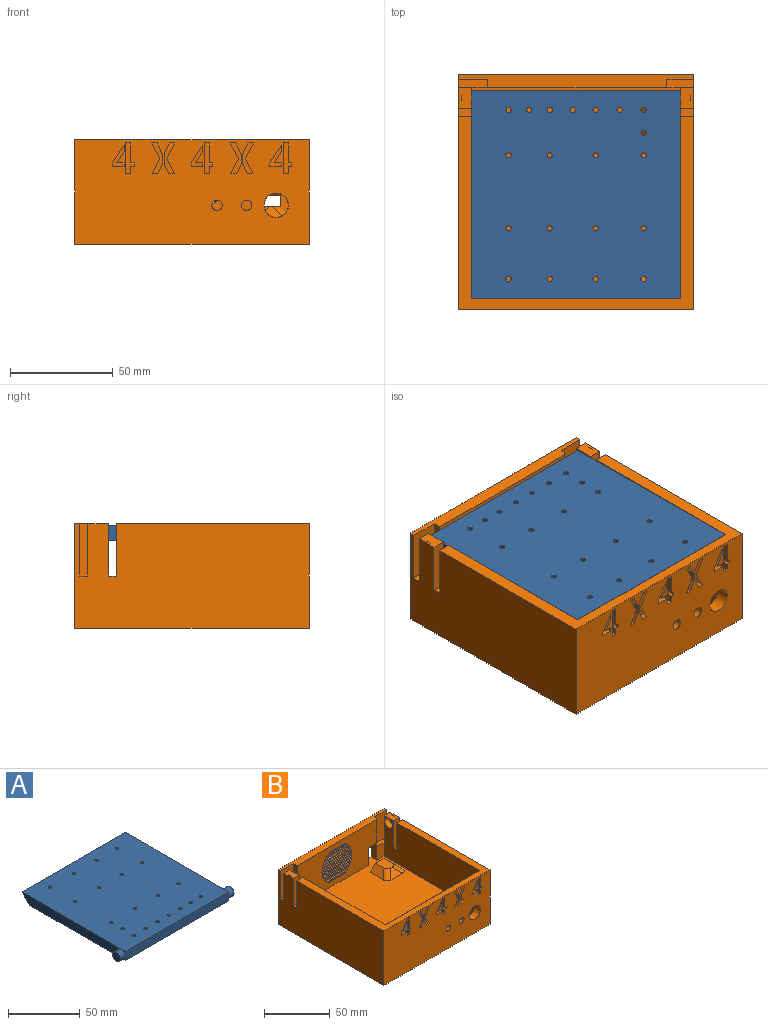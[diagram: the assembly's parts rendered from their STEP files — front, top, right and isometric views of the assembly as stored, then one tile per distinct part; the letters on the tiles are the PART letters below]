
ASSEMBLY  parts=2 mates=1
PART A: 34 faces, bbox 111.8x101.6x7.6 mm
  f0: plane 3.81x3.81mm, normal (-1,0,0), area 3.1mm2, adj f5,f24,f31
  f1: plane 3.81x3.81mm, normal (-1,0,0), area 3.1mm2, adj f5,f23,f31
  f2: plane 3.81x3.81mm, normal (1,0,0), area 3.1mm2, adj f5,f24,f30
  f3: plane 3.81x3.81mm, normal (1,0,0), area 3.1mm2, adj f5,f23,f30
  f4: plane 97.79x7.62mm, normal (-1,0,0), area 693.3mm2, adj f23,f24,f31,f33
  f5: plane 101.6x7.62mm, normal (0,-1,0), area 774.2mm2, adj f0,f1,f2,f3,f23,f24
  f6: plane 97.79x7.62mm, normal (1,0,0), area 693.3mm2, adj f23,f24,f30,f33
  f7: cylinder r=1.27mm len=7.62mm, axis (0,0,-1), area 60.8mm2, adj f23,f24
  f8: cylinder r=1.27mm len=7.62mm, axis (0,0,-1), area 60.8mm2, adj f23,f24
  f9: cylinder r=1.27mm len=7.62mm, axis (0,0,-1), area 60.8mm2, adj f23,f24
  f10: cylinder r=1.27mm len=7.62mm, axis (0,0,-1), area 60.8mm2, adj f23,f24
  f11: cylinder r=1.27mm len=7.62mm, axis (0,0,-1), area 60.8mm2, adj f23,f24
  f12: cylinder r=1.27mm len=7.62mm, axis (0,0,-1), area 60.8mm2, adj f23,f24
  f13: cylinder r=1.27mm len=7.62mm, axis (0,0,-1), area 60.8mm2, adj f23,f24
  f14: cylinder r=1.27mm len=7.62mm, axis (0,0,-1), area 60.8mm2, adj f23,f24
  f15: cylinder r=1.27mm len=7.62mm, axis (0,0,-1), area 60.8mm2, adj f23,f24
  f16: cylinder r=1.27mm len=7.62mm, axis (0,0,-1), area 60.8mm2, adj f23,f24
  f17: cylinder r=1.27mm len=7.62mm, axis (0,0,-1), area 60.8mm2, adj f23,f24
  f18: cylinder r=1.27mm len=7.62mm, axis (0,0,-1), area 60.8mm2, adj f23,f24
  f19: cylinder r=1.27mm len=7.62mm, axis (0,0,-1), area 60.8mm2, adj f23,f24
  f20: cylinder r=1.27mm len=7.62mm, axis (0,0,-1), area 60.8mm2, adj f23,f24
  f21: cylinder r=1.27mm len=7.62mm, axis (0,0,-1), area 60.8mm2, adj f23,f24
  f22: cylinder r=1.27mm len=7.62mm, axis (0,0,-1), area 60.8mm2, adj f23,f24
  f23: plane 101.6x101.6mm, normal (0,0,1), area 10221.2mm2, adj f1,f3,f4,f5,f6,f7,f8,f9
  f24: plane 101.6x93.98mm, normal (0,0,-1), area 9447mm2, adj f0,f2,f4,f5,f6,f7,f8,f9
  f25: cylinder r=1.27mm len=7.62mm, axis (0,0,1), area 60.8mm2, adj f23,f24
  f26: cylinder r=1.27mm len=7.62mm, axis (0,0,1), area 60.8mm2, adj f23,f24
  f27: cylinder r=1.27mm len=7.62mm, axis (0,0,1), area 60.8mm2, adj f23,f24
  f28: cylinder r=1.27mm len=7.62mm, axis (0,0,1), area 60.8mm2, adj f23,f24
  f29: plane 7.62x7.62mm, normal (1,0,0), area 45.6mm2, adj f30
  f30: cylinder r=3.81mm len=7.62mm, axis (1,0,0), area 121.6mm2, adj f2,f3,f6,f29
  f31: cylinder r=3.81mm len=7.62mm, axis (1,0,0), area 121.6mm2, adj f0,f1,f4,f32
  f32: plane 7.62x7.62mm, normal (-1,0,0), area 45.6mm2, adj f31
  f33: plane 101.6x7.62mm, normal (0,0.71,-0.71), area 1094.9mm2, adj f4,f6,f23,f24
PART B: 226 faces, bbox 114.3x114.3x50.8 mm
  f0: plane 100.33x33.02mm, normal (0,1,0), area 3010.1mm2, adj f1,f2,f8,f12,f54,f199,f200,f202
  f1: plane 8.71x5.08mm, normal (1,0,0), area 27.1mm2, adj f0,f203,f204,f212,f225
  f2: plane 8.71x5.08mm, normal (-1,0,0), area 27.1mm2, adj f0,f206,f213,f214,f225
  f3: plane 114.3x50.8mm, normal (-1,0,0), area 5612.9mm2, adj f4,f5,f9,f11,f15,f24,f42,f43
  f4: plane 114.3x6.35mm, normal (0,0,1), area 622.1mm2, adj f3,f7,f11,f23,f45,f53,f221,f222
  f5: plane 114.3x93.98mm, normal (0,0,1), area 1709.7mm2, adj f3,f6,f9,f12,f23,f55,f220,f223
  f6: plane 102.87x38.1mm, normal (-1,0,0), area 3595.4mm2, adj f5,f8,f10,f14,f40,f41,f47,f51
  f7: plane 93.81x38.1mm, normal (0,-1,0), area 2739.9mm2, adj f4,f8,f12,f30,f31,f45,f46,f53
  f8: plane 107.95x101.6mm, normal (0,0,1), area 9676.6mm2, adj f0,f6,f7,f10,f11,f12,f17,f18
  f9: plane 114.3x50.8mm, normal (0,-1,0), area 5314mm2, adj f3,f5,f23,f24,f114,f115,f116,f117
  f10: plane 12.7x7.62mm, normal (0,-1,0), area 96.8mm2, adj f6,f8,f48,f57
  f11: plane 114.3x50.8mm, normal (0,1,0), area 5036.6mm2, adj f3,f4,f8,f23,f24,f34,f35,f36
  f12: plane 103.89x38.1mm, normal (1,0,0), area 3711.9mm2, adj f0,f5,f7,f8,f15,f30,f32,f42
  f13: plane 14.35x11.43mm, normal (0,1,0), area 127.3mm2, adj f201,f205,f218,f225
  f14: plane 10.16x6.35mm, normal (0,0,1), area 64.5mm2, adj f6,f23,f40,f47
  f15: plane 10.16x6.35mm, normal (0,0,1), area 64.5mm2, adj f3,f12,f42,f44
  f16: plane 1.27x0.64mm, normal (0,0,-1), area 0.8mm2, adj f17,f22,f32,f33
  f17: plane 2.03x1.27mm, normal (1,0,0), area 2.6mm2, adj f8,f16,f32,f33
  f18: plane 2.03x1.27mm, normal (-1,0,0), area 2.6mm2, adj f8,f19,f32,f33
  f19: plane 1.27x0.64mm, normal (0,0,-1), area 0.8mm2, adj f18,f20,f32,f33
  f20: plane 2.03x1.27mm, normal (-1,0,0), area 2.6mm2, adj f19,f21,f32,f33
  f21: plane 6.35x1.27mm, normal (0,0,-1), area 8.1mm2, adj f20,f22,f32,f33
  f22: plane 2.03x1.27mm, normal (1,0,0), area 2.6mm2, adj f16,f21,f32,f33
  f23: plane 114.3x50.8mm, normal (1,0,0), area 5612.9mm2, adj f4,f5,f9,f11,f14,f24,f40,f41
  f24: plane 114.3x114.3mm, normal (0,0,-1), area 13064.5mm2, adj f3,f9,f11,f23
  f25: plane 7.87x7.62mm, normal (0,-1,0), area 60mm2, adj f8,f26,f28,f29
  f26: plane 7.87x4.83mm, normal (1,0,0), area 38mm2, adj f8,f25,f27,f29
  f27: plane 7.87x7.62mm, normal (0,1,0), area 60mm2, adj f8,f26,f28,f29
  f28: plane 7.87x4.83mm, normal (-1,0,0), area 38mm2, adj f8,f25,f27,f29
  f29: plane 7.62x4.83mm, normal (0,0,1), area 36.8mm2, adj f25,f26,f27,f28
  f30: plane 18.03x1.02mm, normal (0,0,-1), area 18.3mm2, adj f7,f12,f31,f32
  f31: plane 6.1x1.02mm, normal (-1,0,0), area 6.2mm2, adj f7,f8,f30,f32
  f32: plane 18.03x6.1mm, normal (0,-1,0), area 81.5mm2, adj f8,f12,f16,f17,f18,f19,f20,f21
  f33: plane 10.58x7.24mm, normal (0,1,0), area 35.8mm2, adj f8,f16,f17,f18,f19,f20,f21,f22
  f34: torus R=8.79mm, axis (0,-1,0), area 62.2mm2, adj f11,f33,f35,f36
  f35: cylinder r=5.08mm len=4.98mm, axis (-1,0,0), area 20.7mm2, adj f11,f33,f34,f37
  f36: torus R=8.79mm, axis (0,-1,0), area 62.2mm2, adj f11,f33,f34,f38
  f37: torus R=8.79mm, axis (0,-1,0), area 62.2mm2, adj f11,f33,f35,f39
  f38: cylinder r=5.08mm len=4.98mm, axis (-1,0,0), area 20.7mm2, adj f11,f33,f36,f39
  f39: torus R=8.79mm, axis (0,-1,0), area 62.2mm2, adj f11,f33,f37,f38
  f40: plane 25.4x6.35mm, normal (0,-1,0), area 161.3mm2, adj f6,f14,f23,f41
  f41: plane 6.35x3.81mm, normal (0,0,1), area 24.2mm2, adj f6,f23,f40,f220
  f42: plane 25.4x6.35mm, normal (0,-1,0), area 161.3mm2, adj f3,f12,f15,f43
  f43: plane 6.35x3.81mm, normal (0,0,1), area 24.2mm2, adj f3,f12,f42,f223
  f44: plane 25.4x6.35mm, normal (0,1,0), area 161.3mm2, adj f3,f12,f15,f46
  f45: plane 25.4x3.81mm, normal (-1,0,0), area 96.8mm2, adj f4,f7,f46,f224
  f46: plane 14.14x3.81mm, normal (0,0,1), area 53.9mm2, adj f3,f7,f44,f45,f224
  f47: plane 25.4x6.35mm, normal (0,1,0), area 161.3mm2, adj f6,f14,f23,f48
  f48: plane 13.97x3.81mm, normal (0,0,1), area 49.8mm2, adj f10,f23,f47,f53,f57,f221,f222
  f49: plane 8.89x8.89mm, normal (1,0,0), area 62.1mm2, adj f50
  f50: cylinder r=4.45mm len=8.89mm, axis (-1,0,0), area 141.9mm2, adj f12,f49
  f51: cylinder r=4.45mm len=8.89mm, axis (-1,0,0), area 141.9mm2, adj f6,f52
  f52: plane 8.89x8.89mm, normal (-1,0,0), area 62.1mm2, adj f51
  f53: plane 25.4x1.27mm, normal (0.71,-0.71,0), area 44.9mm2, adj f4,f7,f48,f57,f219,f221
  f54: plane 101.6x3.81mm, normal (0,0,-1), area 386.7mm2, adj f0,f6,f12,f55,f216
  f55: plane 101.6x5.08mm, normal (0,0.71,0.71), area 729.9mm2, adj f5,f6,f12,f54
  f56: plane 9.14x1.27mm, normal (0,0,-1), area 11.6mm2, adj f11,f57,f58,f219
  f57: plane 15.83x6.35mm, normal (-1,0,0), area 81.7mm2, adj f8,f10,f11,f48,f53,f56,f219
  f58: plane 16x6.35mm, normal (1,0,0), area 82.3mm2, adj f7,f8,f11,f56,f219
  f59: plane 20.32x5.59mm, normal (0,1,0), area 82.3mm2, adj f8,f60,f62,f63
  f60: plane 12.7x9.14mm, normal (0,0,1), area 110.3mm2, adj f59,f61,f62,f63,f64,f65
  f61: plane 12.42x5.59mm, normal (0,-0.71,0.71), area 54mm2, adj f8,f60,f64,f65
  f62: plane 14.34x5.59mm, normal (0.71,0,0.71), area 91.2mm2, adj f8,f59,f60,f65
  f63: plane 14.34x5.59mm, normal (-0.71,0,0.71), area 91.2mm2, adj f8,f59,f60,f64
  f64: cylinder r=5.59mm len=10.15mm, axis (-0.58,-0.58,-0.58), area 56.6mm2, adj f8,f60,f61,f63
  f65: cylinder r=5.59mm len=10.15mm, axis (0.58,-0.58,-0.58), area 56.6mm2, adj f8,f60,f61,f62
  f66: plane 15.95x6.35mm, normal (0,0,1), area 101.3mm2, adj f7,f11,f67,f69
  f67: cylinder r=16.09mm len=6.35mm, axis (0,-1,0), area 7.6mm2, adj f7,f11,f66,f68
  f68: plane 17.99x6.35mm, normal (0,0,-1), area 114.2mm2, adj f7,f11,f67,f69
  f69: cylinder r=16.09mm len=6.35mm, axis (0,-1,0), area 7.6mm2, adj f7,f11,f66,f68
  f70: plane 23.85x6.35mm, normal (0,0,-1), area 151.4mm2, adj f7,f11,f71,f73
  f71: cylinder r=16.09mm len=6.35mm, axis (0,-1,0), area 11.5mm2, adj f7,f11,f70,f72
  f72: plane 21.28x6.35mm, normal (0,0,1), area 135.1mm2, adj f7,f11,f71,f73
  f73: cylinder r=16.09mm len=6.35mm, axis (0,-1,0), area 11.5mm2, adj f7,f11,f70,f72
  f74: plane 25.92x6.35mm, normal (0,0,1), area 164.6mm2, adj f7,f11,f75,f77
  f75: cylinder r=16.09mm len=6.35mm, axis (0,-1,0), area 9.7mm2, adj f7,f11,f74,f76
  f76: plane 27.61x6.35mm, normal (0,0,-1), area 175.3mm2, adj f7,f11,f75,f77
  f77: cylinder r=16.09mm len=6.35mm, axis (0,-1,0), area 9.7mm2, adj f7,f11,f74,f76
  f78: cylinder r=16.09mm len=6.35mm, axis (0,-1,0), area 8.8mm2, adj f7,f11,f79,f81
  f79: plane 28.98x6.35mm, normal (0,0,1), area 184mm2, adj f7,f11,f78,f80
  f80: cylinder r=16.09mm len=6.35mm, axis (0,-1,0), area 8.8mm2, adj f7,f11,f79,f81
  f81: plane 30.07x6.35mm, normal (0,0,-1), area 191mm2, adj f7,f11,f78,f80
  f82: plane 31.54x6.35mm, normal (0,0,-1), area 200.3mm2, adj f7,f11,f83,f85
  f83: cylinder r=16.09mm len=6.35mm, axis (0,-1,0), area 8.3mm2, adj f7,f11,f82,f84
  f84: plane 30.92x6.35mm, normal (0,0,1), area 196.3mm2, adj f7,f11,f83,f85
  f85: cylinder r=16.09mm len=6.35mm, axis (0,-1,0), area 8.3mm2, adj f7,f11,f82,f84
  f86: plane 31.94x6.35mm, normal (0,0,1), area 202.8mm2, adj f7,f11,f87,f89
  f87: cylinder r=16.09mm len=6.35mm, axis (0,-1,0), area 8.1mm2, adj f7,f11,f86,f88
  f88: plane 32.15x6.35mm, normal (0,0,-1), area 204.1mm2, adj f7,f11,f87,f89
  f89: cylinder r=16.09mm len=6.35mm, axis (0,-1,0), area 8.1mm2, adj f7,f11,f86,f88
  f90: plane 32.15x6.35mm, normal (0,0,1), area 204.1mm2, adj f7,f11,f91,f93
  f91: cylinder r=16.09mm len=6.35mm, axis (0,-1,0), area 8.1mm2, adj f7,f11,f90,f92
  f92: plane 31.94x6.35mm, normal (0,0,-1), area 202.8mm2, adj f7,f11,f91,f93
  f93: cylinder r=16.09mm len=6.35mm, axis (0,-1,0), area 8.1mm2, adj f7,f11,f90,f92
  f94: plane 30.92x6.35mm, normal (0,0,-1), area 196.3mm2, adj f7,f11,f95,f97
  f95: cylinder r=16.09mm len=6.35mm, axis (0,-1,0), area 8.3mm2, adj f7,f11,f94,f96
  f96: plane 31.54x6.35mm, normal (0,0,1), area 200.3mm2, adj f7,f11,f95,f97
  f97: cylinder r=16.09mm len=6.35mm, axis (0,-1,0), area 8.3mm2, adj f7,f11,f94,f96
  f98: plane 30.07x6.35mm, normal (0,0,1), area 191mm2, adj f7,f11,f99,f101
  f99: cylinder r=16.09mm len=6.35mm, axis (0,-1,0), area 8.8mm2, adj f7,f11,f98,f100
  f100: plane 28.98x6.35mm, normal (0,0,-1), area 184mm2, adj f7,f11,f99,f101
  f101: cylinder r=16.09mm len=6.35mm, axis (0,-1,0), area 8.8mm2, adj f7,f11,f98,f100
  f102: cylinder r=16.09mm len=6.35mm, axis (0,-1,0), area 9.7mm2, adj f7,f11,f103,f105
  f103: plane 27.61x6.35mm, normal (0,0,1), area 175.3mm2, adj f7,f11,f102,f104
  f104: cylinder r=16.09mm len=6.35mm, axis (0,-1,0), area 9.7mm2, adj f7,f11,f103,f105
  f105: plane 25.92x6.35mm, normal (0,0,-1), area 164.6mm2, adj f7,f11,f102,f104
  f106: plane 21.28x6.35mm, normal (0,0,-1), area 135.1mm2, adj f7,f11,f107,f109
  f107: cylinder r=16.09mm len=6.35mm, axis (0,-1,0), area 11.5mm2, adj f7,f11,f106,f108
  f108: plane 23.85x6.35mm, normal (0,0,1), area 151.4mm2, adj f7,f11,f107,f109
  f109: cylinder r=16.09mm len=6.35mm, axis (0,-1,0), area 11.5mm2, adj f7,f11,f106,f108
  f110: plane 15.95x6.35mm, normal (0,0,-1), area 101.3mm2, adj f7,f11,f111,f113
  f111: cylinder r=16.09mm len=6.35mm, axis (0,-1,0), area 7.6mm2, adj f7,f11,f110,f112
  f112: plane 17.99x6.35mm, normal (0,0,1), area 114.2mm2, adj f7,f11,f111,f113
  f113: cylinder r=16.09mm len=6.35mm, axis (0,-1,0), area 7.6mm2, adj f7,f11,f110,f112
  f114: plane 7.76x4.07mm, normal (-0.89,0,0.46), area 22.3mm2, adj f9,f115,f120,f121
  f115: plane 2.81x2.54mm, normal (0,0,-1), area 7.1mm2, adj f9,f114,f116,f121
  f116: plane 5.24x2.54mm, normal (0.91,0,-0.42), area 14.7mm2, adj f9,f115,f117,f121
  f117: plane 4.67x2.54mm, normal (1,0,0), area 11.9mm2, adj f9,f116,f118,f121
  f118: plane 5.18x2.54mm, normal (0.92,0,0.39), area 14.3mm2, adj f9,f117,f119,f121
  f119: plane 2.85x2.54mm, normal (0,0,1), area 7.2mm2, adj f9,f118,f120,f121
  f120: plane 7.34x3.83mm, normal (-0.89,0,-0.46), area 21mm2, adj f9,f114,f119,f121
  f121: plane 15.1x5.26mm, normal (0,-1,0), area 35.7mm2, adj f114,f115,f116,f117,f118,f119,f120
  f122: plane 2.81x2.54mm, normal (0,0,-1), area 7.1mm2, adj f9,f123,f128,f129
  f123: plane 7.76x4.07mm, normal (0.89,0,0.46), area 22.3mm2, adj f9,f122,f124,f129
  f124: plane 7.34x3.83mm, normal (0.89,0,-0.46), area 21mm2, adj f9,f123,f125,f129
  f125: plane 2.85x2.54mm, normal (0,0,1), area 7.2mm2, adj f9,f124,f126,f129
  f126: plane 4.75x2.54mm, normal (-0.91,0,0.42), area 13.3mm2, adj f9,f125,f127,f129
  f127: plane 4.69x2.54mm, normal (-1,0,0), area 11.9mm2, adj f9,f126,f128,f129
  f128: plane 5.65x2.54mm, normal (-0.92,0,-0.4), area 15.7mm2, adj f9,f122,f127,f129
  f129: plane 15.1x5.26mm, normal (0,-1,0), area 35.7mm2, adj f122,f123,f124,f125,f126,f127,f128
  f130: plane 2.54x1.58mm, normal (0,0,-1), area 4mm2, adj f9,f131,f137,f138
  f131: plane 9.63x2.54mm, normal (-1,0,0), area 24.5mm2, adj f9,f130,f132,f138
  f132: plane 2.54x2.5mm, normal (0,0,-1), area 6.4mm2, adj f9,f131,f133,f138
  f133: plane 15.1x2.54mm, normal (1,0,0), area 38.3mm2, adj f9,f132,f134,f138
  f134: plane 2.54x2.5mm, normal (0,0,1), area 6.4mm2, adj f9,f133,f135,f138
  f135: plane 3.52x2.54mm, normal (-1,0,0), area 8.9mm2, adj f9,f134,f136,f138
  f136: plane 2.54x1.58mm, normal (0,0,1), area 4mm2, adj f9,f135,f137,f138
  f137: plane 2.54x1.95mm, normal (-1,0,0), area 4.9mm2, adj f9,f130,f136,f138
  f138: plane 15.1x4.08mm, normal (0,-1,0), area 40.8mm2, adj f130,f131,f132,f133,f134,f135,f136,f137
  f139: plane 2.54x1.95mm, normal (1,0,0), area 4.9mm2, adj f9,f140,f145,f146
  f140: plane 5.69x2.54mm, normal (0,0,1), area 14.5mm2, adj f9,f139,f141,f146
  f141: plane 2.54x1.95mm, normal (-1,0,0), area 4.9mm2, adj f9,f140,f142,f146
  f142: plane 3.5x2.54mm, normal (0,0,-1), area 8.9mm2, adj f9,f141,f143,f146
  f143: plane 5.47x3.5mm, normal (-0.84,0,0.54), area 16.5mm2, adj f9,f142,f144,f146
  f144: plane 2.93x2.54mm, normal (-1,0,0), area 7.4mm2, adj f9,f143,f145,f146
  f145: plane 8.4x5.69mm, normal (0.83,0,-0.56), area 25.8mm2, adj f9,f139,f144,f146
  f146: plane 10.34x5.69mm, normal (0,-1,0), area 25.4mm2, adj f139,f140,f141,f142,f143,f144,f145
  f147: plane 2.54x1.95mm, normal (1,0,0), area 4.9mm2, adj f9,f148,f153,f154
  f148: plane 5.69x2.54mm, normal (0,0,1), area 14.5mm2, adj f9,f147,f149,f154
  f149: plane 2.54x1.95mm, normal (-1,0,0), area 4.9mm2, adj f9,f148,f150,f154
  f150: plane 3.5x2.54mm, normal (0,0,-1), area 8.9mm2, adj f9,f149,f151,f154
  f151: plane 5.47x3.5mm, normal (-0.84,0,0.54), area 16.5mm2, adj f9,f150,f152,f154
  f152: plane 2.93x2.54mm, normal (-1,0,0), area 7.4mm2, adj f9,f151,f153,f154
  f153: plane 8.4x5.69mm, normal (0.83,0,-0.56), area 25.8mm2, adj f9,f147,f152,f154
  f154: plane 10.34x5.69mm, normal (0,-1,0), area 25.4mm2, adj f147,f148,f149,f150,f151,f152,f153
  f155: plane 7.76x4.07mm, normal (-0.89,0,0.46), area 22.3mm2, adj f9,f156,f161,f162
  f156: plane 2.81x2.54mm, normal (0,0,-1), area 7.1mm2, adj f9,f155,f157,f162
  f157: plane 5.24x2.54mm, normal (0.91,0,-0.42), area 14.7mm2, adj f9,f156,f158,f162
  f158: plane 4.67x2.54mm, normal (1,0,0), area 11.9mm2, adj f9,f157,f159,f162
  f159: plane 5.18x2.54mm, normal (0.92,0,0.39), area 14.3mm2, adj f9,f158,f160,f162
  f160: plane 2.85x2.54mm, normal (0,0,1), area 7.2mm2, adj f9,f159,f161,f162
  f161: plane 7.34x3.83mm, normal (-0.89,0,-0.46), area 21mm2, adj f9,f155,f160,f162
  f162: plane 15.1x5.26mm, normal (0,-1,0), area 35.7mm2, adj f155,f156,f157,f158,f159,f160,f161
  f163: plane 2.54x1.95mm, normal (1,0,0), area 4.9mm2, adj f9,f164,f169,f170
  f164: plane 5.69x2.54mm, normal (0,0,1), area 14.5mm2, adj f9,f163,f165,f170
  f165: plane 2.54x1.95mm, normal (-1,0,0), area 4.9mm2, adj f9,f164,f166,f170
  f166: plane 3.5x2.54mm, normal (0,0,-1), area 8.9mm2, adj f9,f165,f167,f170
  f167: plane 5.47x3.5mm, normal (-0.84,0,0.54), area 16.5mm2, adj f9,f166,f168,f170
  f168: plane 2.93x2.54mm, normal (-1,0,0), area 7.4mm2, adj f9,f167,f169,f170
  f169: plane 8.4x5.69mm, normal (0.83,0,-0.56), area 25.8mm2, adj f9,f163,f168,f170
  f170: plane 10.34x5.69mm, normal (0,-1,0), area 25.4mm2, adj f163,f164,f165,f166,f167,f168,f169
  f171: plane 2.54x1.58mm, normal (0,0,-1), area 4mm2, adj f9,f172,f178,f179
  f172: plane 9.63x2.54mm, normal (-1,0,0), area 24.5mm2, adj f9,f171,f173,f179
  f173: plane 2.54x2.5mm, normal (0,0,-1), area 6.4mm2, adj f9,f172,f174,f179
  f174: plane 15.1x2.54mm, normal (1,0,0), area 38.3mm2, adj f9,f173,f175,f179
  f175: plane 2.54x2.5mm, normal (0,0,1), area 6.4mm2, adj f9,f174,f176,f179
  f176: plane 3.52x2.54mm, normal (-1,0,0), area 8.9mm2, adj f9,f175,f177,f179
  f177: plane 2.54x1.58mm, normal (0,0,1), area 4mm2, adj f9,f176,f178,f179
  f178: plane 2.54x1.95mm, normal (-1,0,0), area 4.9mm2, adj f9,f171,f177,f179
  f179: plane 15.1x4.08mm, normal (0,-1,0), area 40.8mm2, adj f171,f172,f173,f174,f175,f176,f177,f178
  f180: plane 2.81x2.54mm, normal (0,0,-1), area 7.1mm2, adj f9,f181,f186,f187
  f181: plane 7.76x4.07mm, normal (0.89,0,0.46), area 22.3mm2, adj f9,f180,f182,f187
  f182: plane 7.34x3.83mm, normal (0.89,0,-0.46), area 21mm2, adj f9,f181,f183,f187
  f183: plane 2.85x2.54mm, normal (0,0,1), area 7.2mm2, adj f9,f182,f184,f187
  f184: plane 4.75x2.54mm, normal (-0.91,0,0.42), area 13.3mm2, adj f9,f183,f185,f187
  f185: plane 4.69x2.54mm, normal (-1,0,0), area 11.9mm2, adj f9,f184,f186,f187
  f186: plane 5.65x2.54mm, normal (-0.92,0,-0.4), area 15.7mm2, adj f9,f180,f185,f187
  f187: plane 15.1x5.26mm, normal (0,-1,0), area 35.7mm2, adj f180,f181,f182,f183,f184,f185,f186
  f188: plane 2.54x1.58mm, normal (0,0,-1), area 4mm2, adj f9,f189,f195,f196
  f189: plane 9.63x2.54mm, normal (-1,0,0), area 24.5mm2, adj f9,f188,f190,f196
  f190: plane 2.54x2.5mm, normal (0,0,-1), area 6.4mm2, adj f9,f189,f191,f196
  f191: plane 15.1x2.54mm, normal (1,0,0), area 38.3mm2, adj f9,f190,f192,f196
  f192: plane 2.54x2.5mm, normal (0,0,1), area 6.4mm2, adj f9,f191,f193,f196
  f193: plane 3.52x2.54mm, normal (-1,0,0), area 8.9mm2, adj f9,f192,f194,f196
  f194: plane 2.54x1.58mm, normal (0,0,1), area 4mm2, adj f9,f193,f195,f196
  f195: plane 2.54x1.95mm, normal (-1,0,0), area 4.9mm2, adj f9,f188,f194,f196
  f196: plane 15.1x4.08mm, normal (0,-1,0), area 40.8mm2, adj f188,f189,f190,f191,f192,f193,f194,f195
  f197: cylinder r=2.54mm len=5.84mm, axis (0,-1,0), area 93.2mm2, adj f9,f199
  f198: cylinder r=2.54mm len=5.84mm, axis (0,-1,0), area 93.2mm2, adj f9,f200
  f199: cone r=3.05mm half-angle=45deg, axis (0,1,0), area 12.6mm2, adj f0,f197
  f200: cone r=3.05mm half-angle=45deg, axis (0,1,0), area 12.6mm2, adj f0,f198
  f201: plane 17.08x14.35mm, normal (1,0,0), area 195mm2, adj f8,f13,f207,f217,f218,f225
  f202: plane 11.41x2.54mm, normal (-1,0,0), area 22.1mm2, adj f0,f208,f211,f212
  f203: plane 3.56x1.02mm, normal (0,0,1), area 3mm2, adj f1,f204,f211,f212
  f204: plane 7.35x1.52mm, normal (0,1,0), area 10.8mm2, adj f1,f203,f207,f211,f225
  f205: plane 17.08x14.35mm, normal (-1,0,0), area 195mm2, adj f8,f13,f209,f217,f218,f225
  f206: plane 11.41x4.06mm, normal (0,1,0), area 33mm2, adj f2,f6,f209,f214,f225
  f207: cylinder r=5.08mm len=9.14mm, axis (-1,0,0), area 34.2mm2, adj f8,f201,f204,f210,f225
  f208: cylinder r=5.08mm len=10.16mm, axis (0,-1,0), area 42.4mm2, adj f0,f8,f202,f210
  f209: cylinder r=5.08mm len=5.08mm, axis (-1,0,0), area 32.4mm2, adj f6,f8,f205,f206,f225
  f210: bspline ~7.62x7.62mm, area 23.3mm2, adj f207,f208,f211
  f211: cylinder r=2.54mm len=7.65mm, axis (0,0,-1), area 29.5mm2, adj f202,f203,f204,f210,f212
  f212: cylinder r=4.06mm len=4.06mm, axis (-1,0,0), area 25.7mm2, adj f0,f1,f202,f203,f211
  f213: cylinder r=4.06mm len=4.06mm, axis (-1,0,0), area 11.4mm2, adj f0,f2,f215
  f214: cylinder r=4.06mm len=4.06mm, axis (0,1,0), area 17.8mm2, adj f2,f6,f206,f215
  f215: bspline ~4.76x4.06mm, area 8.7mm2, adj f213,f214,f216
  f216: cylinder r=1.27mm len=16.53mm, axis (0,0,1), area 33mm2, adj f0,f6,f54,f215
  f217: plane 11.43x9.71mm, normal (0,-1,0), area 111mm2, adj f8,f201,f205,f218
  f218: plane 17.08x11.43mm, normal (0,0,1), area 195.3mm2, adj f13,f201,f205,f217
  f219: plane 9.14x5.08mm, normal (0,-0.71,-0.71), area 65.7mm2, adj f7,f53,f56,f57,f58
  f220: plane 25.4x6.35mm, normal (0,1,0), area 161.3mm2, adj f5,f6,f23,f41
  f221: plane 25.4x2.54mm, normal (1,0,0), area 64.5mm2, adj f4,f48,f53,f222
  f222: plane 25.4x12.87mm, normal (0,-1,0), area 326.9mm2, adj f4,f23,f48,f221
  f223: plane 25.4x6.35mm, normal (0,1,0), area 161.3mm2, adj f3,f5,f12,f43
  f224: plane 25.4x14.14mm, normal (0,-1,0), area 359.1mm2, adj f3,f4,f45,f46
  f225: cylinder r=5.93mm len=11.86mm, axis (0,-1,0), area 268.8mm2, adj f0,f1,f2,f9,f13,f201,f204,f205
PLACE A rot(axis=(0,0,-1),180deg) t=(127.13,50.76,5.05)mm
PLACE B t=(125.35,47.25,-37.68)mm fixed
MATE revolute A.f30 <-> B.f50  axis (-1,0,0) through (76.79,99.94,8.65)mm
